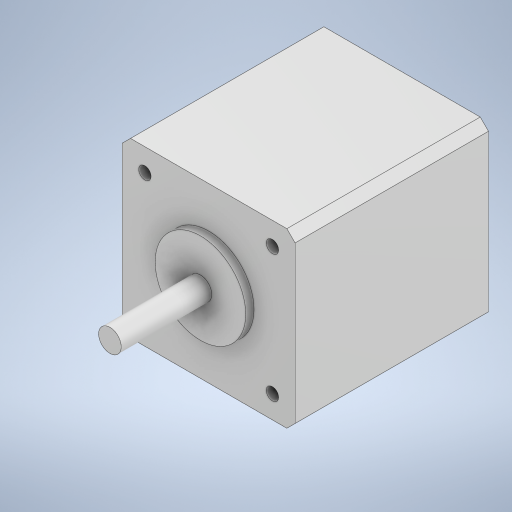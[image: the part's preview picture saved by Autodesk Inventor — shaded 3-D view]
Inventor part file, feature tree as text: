
AUTODESK INVENTOR PART (.ipt)
format: ipt  version: 2024 (Build 280153000, 153)  size: 274,944 bytes
history: native  units: mm
features: extrude x4, sketch x4, projected_geometry x3, plane x2, chamfer x1
ambient origin geometry x8: Origin, YZ Plane, XZ Plane, XY Plane, X Axis, Y Axis, Z Axis, Center Point
bodies: Solid1 (feature_tree)
feature tree (14):
  extrude  "Extrusion1"  Depth=42.0mm
  chamfer  "Chamfer1"  Distance=47.0mm
  extrude  "Extrusion2"  Depth=22.0mm
  extrude  "Extrusion3"  Depth=21.0mm
  extrude  "Extrusion4"  Depth=4.5mm
  plane  "Work Plane1"
  plane  "Work Plane2"
  sketch  "Sketch1"  dims[d0=42.0mm d1=42.0mm d2=47.0mm d3=0.0mm]
  sketch  "Sketch2"  dims[d4=2.0mm d5=2.0mm d6=45.0deg d7=22.0mm]
  sketch  "Sketch3"  dims[d10=21.0mm d11=21.0mm]
  sketch  "Sketch4"  dims[d12=2.0mm d13=0.0mm d14=5.5mm d15=24.0mm d16=0.0mm d17=31.0mm d18=31.0mm d19=3.0mm d20=4.5mm d21=0.0mm]
  projected_geometry  "Projected Loop1"
  projected_geometry  "Projected Loop2"
  projected_geometry  "Projected Loop3"
